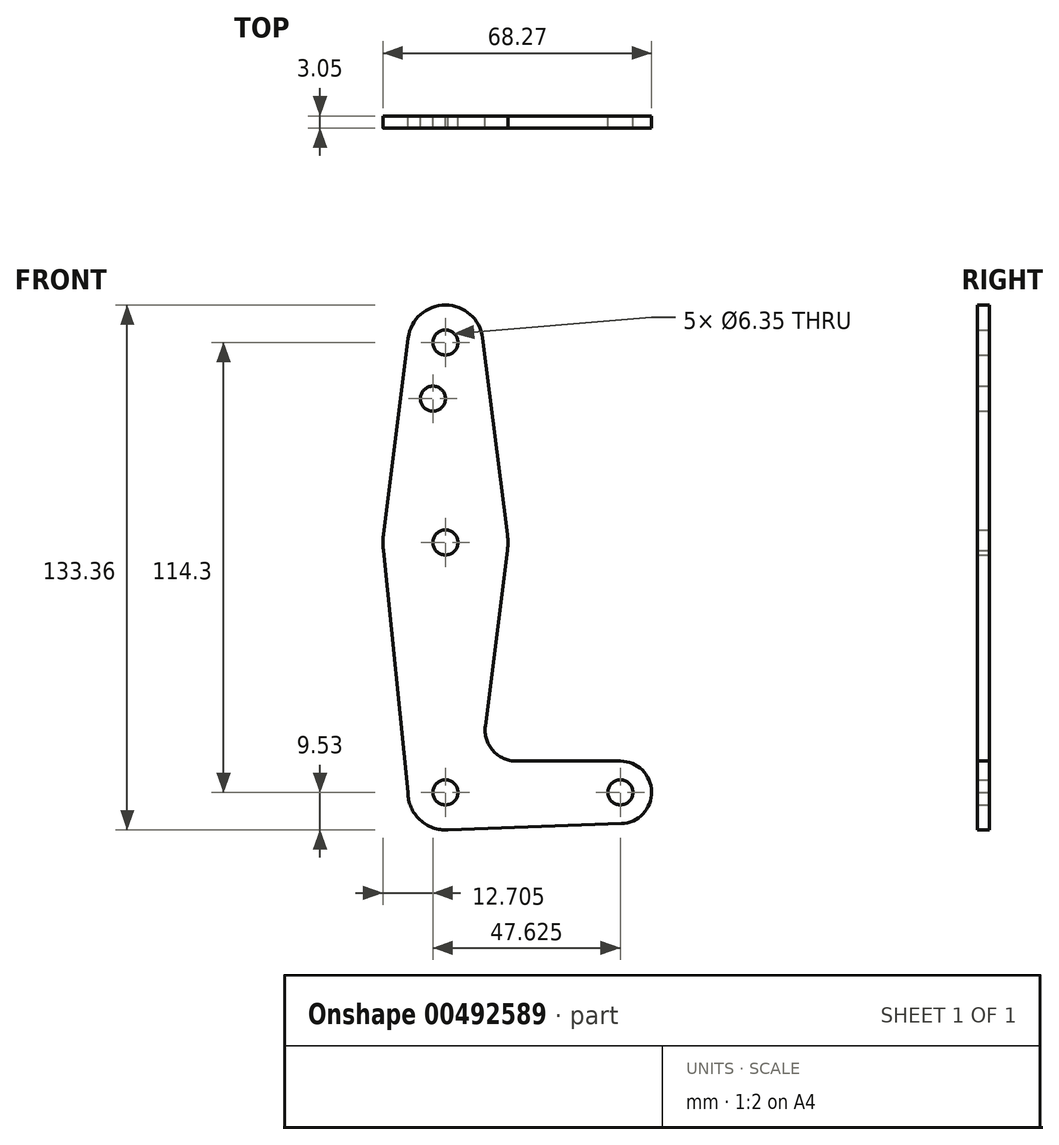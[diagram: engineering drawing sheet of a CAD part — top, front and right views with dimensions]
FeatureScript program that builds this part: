
annotation { "Feature Type Name" : "Feature", "Feature Type Description" : "" }
export const myFeature = defineFeature(function(context is Context, id is Id, definition is map)
    precondition{}
    {
        {
            var Q0;
            Q0=qCreatedBy(makeId("Front.planeOp"),FACE);
            var sketch = newSketch(context, id + "F0", { "sketchPlane" : qUnion([Q0])});
            skLineSegment(sketch, "E0", {"start": v(0, 0) * mm, "end": v(44.45, 0) * mm, "construction": true});
            skCircle(sketch, "E1", {"center": v(0, 114.3) * mm, "radius": 9.53 * mm});
            skCircle(sketch, "E2", {"center": v(0, 63.5) * mm, "radius": 15.88 * mm});
            skCircle(sketch, "E3", {"center": v(0, 0) * mm, "radius": 9.53 * mm});
            skCircle(sketch, "E4", {"center": v(44.45, 0) * mm, "radius": 7.94 * mm});
            skLineSegment(sketch, "E5", {"start": v(0, 0) * mm, "end": v(0, 114.3) * mm, "construction": true});
            skLineSegment(sketch, "E6", {"start": v(-9.45, 115.5) * mm, "end": v(-15.75, 65.48) * mm});
            skLineSegment(sketch, "E7", {"start": v(-15.75, 65.48) * mm, "end": v(-15.75, 61.52) * mm});
            skLineSegment(sketch, "E8", {"start": v(9.45, 115.5) * mm, "end": v(15.75, 65.48) * mm});
            skLineSegment(sketch, "E9", {"start": v(0, -9.53) * mm, "end": v(44.73, -7.93) * mm});
            skCircle(sketch, "E10", {"center": v(0, 114.3) * mm, "radius": 3.18 * mm});
            skCircle(sketch, "E11", {"center": v(0, 63.5) * mm, "radius": 3.18 * mm});
            skCircle(sketch, "E12", {"center": v(0, 0) * mm, "radius": 3.18 * mm});
            skCircle(sketch, "E13", {"center": v(44.45, 0) * mm, "radius": 3.18 * mm});
            skCircle(sketch, "E14", {"center": v(-3.18, 100.03) * mm, "radius": 3.18 * mm});
            skLineSegment(sketch, "E15", {"start": v(-15.75, 61.52) * mm, "end": v(-9.53, 0) * mm});
            skLineSegment(sketch, "E16", {"start": v(15.75, 61.52) * mm, "end": v(10.13, 16.88) * mm});
            skLineSegment(sketch, "E17", {"start": v(18.01, 7.94) * mm, "end": v(44.45, 7.94) * mm});
            skArc(sketch, "E18.filletArc", {"start": v(10.13, 16.88) * mm, "mid": v(12.05, 10.63) * mm, "end": v(18.01, 7.94) * mm});
            skSolve(sketch);
        }
        {
            var Q0;
            Q0 = qSketchRegion(id + "F0", true);
            extrude(context, id + "F1", {"entities" : qUnion([Q0]), "depth" : 3.05 * mm});
        }
    });
